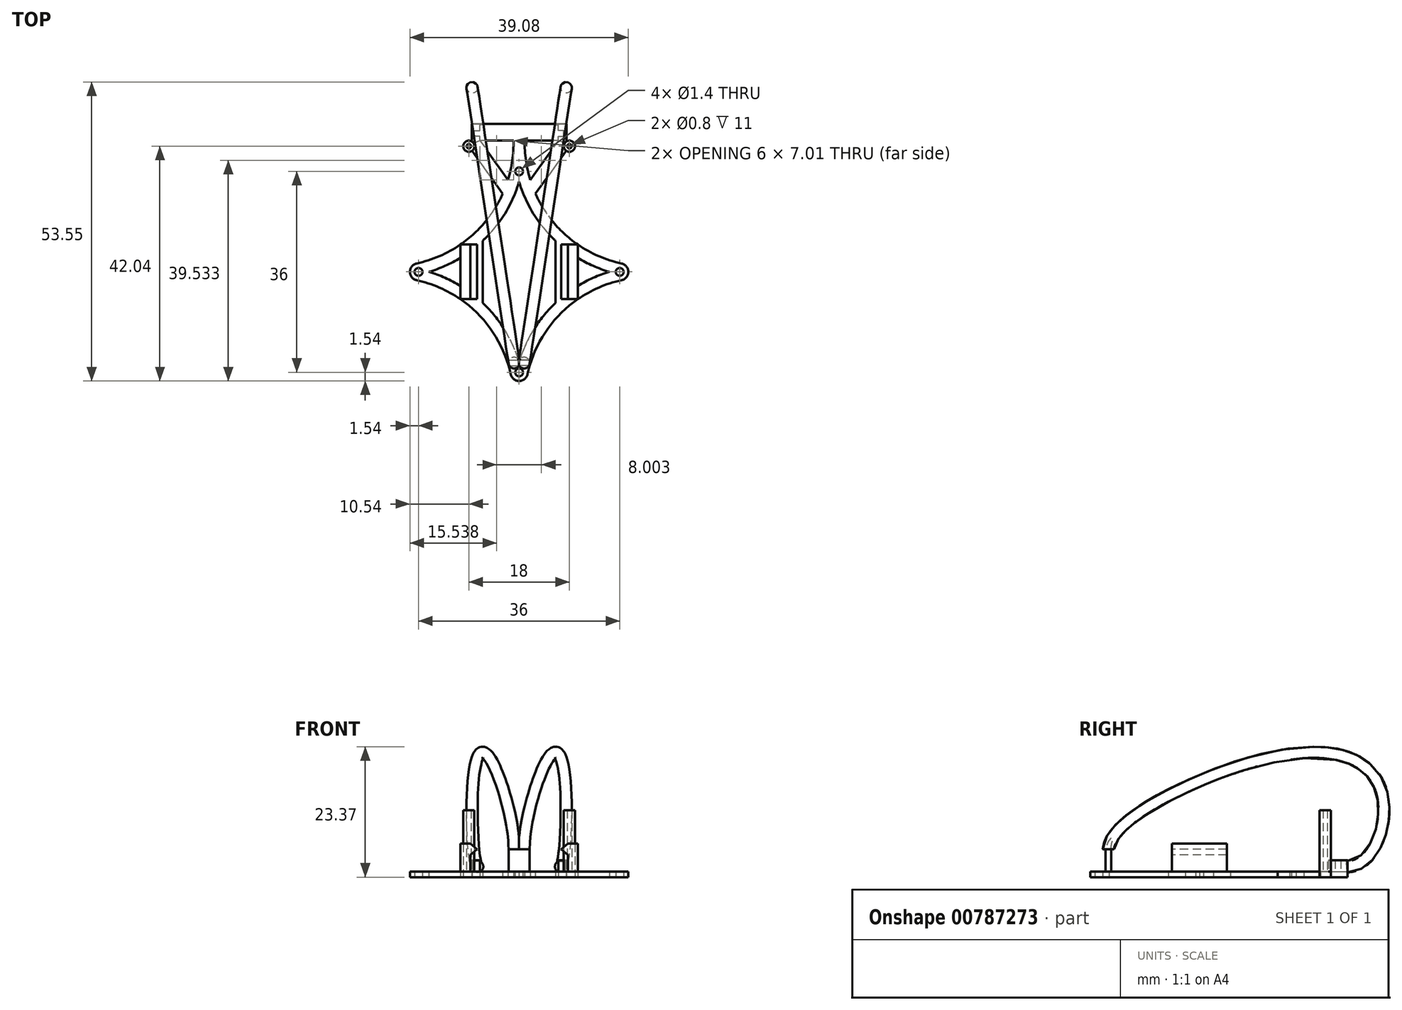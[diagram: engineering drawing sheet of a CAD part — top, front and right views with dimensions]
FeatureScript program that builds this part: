
annotation { "Feature Type Name" : "Feature", "Feature Type Description" : "" }
export const myFeature = defineFeature(function(context is Context, id is Id, definition is map)
    precondition{}
    {
        {
            var Q0;
            Q0=qCreatedBy(makeId("Top.planeOp"),FACE);
            var sketch = newSketch(context, id + "F0", { "sketchPlane" : qUnion([Q0])});
            skCircle(sketch, "E0", {"center": v(0, 18) * mm, "radius": 0.7 * mm});
            skCircle(sketch, "E1", {"center": v(18, 0) * mm, "radius": 0.7 * mm});
            skCircle(sketch, "E2", {"center": v(0, -18) * mm, "radius": 0.7 * mm});
            skCircle(sketch, "E3", {"center": v(-18, 0) * mm, "radius": 0.7 * mm});
            skLineSegment(sketch, "E4.bottom", {"start": v(23, 23) * mm, "end": v(-23, 23) * mm, "construction": true});
            skLineSegment(sketch, "E4.top", {"start": v(23, -23) * mm, "end": v(-23, -23) * mm, "construction": true});
            skLineSegment(sketch, "E4.left", {"start": v(23, 23) * mm, "end": v(23, -23) * mm, "construction": true});
            skLineSegment(sketch, "E4.right", {"start": v(-23, 23) * mm, "end": v(-23, -23) * mm, "construction": true});
            skPoint(sketch, "E4.middle", {"position": v(0, 0) * mm});
            skArc(sketch, "E5", {"start": v(1, 23.5) * mm, "mid": v(1.21, 19.95) * mm, "end": v(1.99, 16.49) * mm});
            skArc(sketch, "E6", {"start": v(18.33, -1.5) * mm, "mid": v(7.44, -7.44) * mm, "end": v(1.5, -18.33) * mm});
            skArc(sketch, "E7", {"start": v(-1.5, -18.33) * mm, "mid": v(-7.44, -7.44) * mm, "end": v(-18.33, -1.5) * mm});
            skArc(sketch, "E8", {"start": v(-18.33, 1.5) * mm, "mid": v(-9.14, 5.92) * mm, "end": v(-2.93, 14) * mm});
            skPoint(sketch, "E9", {"position": v(0, 35.14) * mm});
            skArc(sketch, "E10", {"start": v(0, 16.14) * mm, "mid": v(2.55, 10.43) * mm, "end": v(6.5, 5.57) * mm});
            skArc(sketch, "E11", {"start": v(0, 16.14) * mm, "mid": v(-2.55, 10.43) * mm, "end": v(-6.5, 5.57) * mm});
            skArc(sketch, "E12", {"start": v(-16.14, 0) * mm, "mid": v(-13.24, -1.07) * mm, "end": v(-10.5, -2.51) * mm});
            skArc(sketch, "E13", {"start": v(16.14, 0) * mm, "mid": v(13.24, -1.07) * mm, "end": v(10.5, -2.51) * mm});
            skArc(sketch, "E14", {"start": v(-1.5, -18.33) * mm, "mid": v(0, -19.54) * mm, "end": v(1.5, -18.33) * mm});
            skArc(sketch, "E15", {"start": v(-18.33, -1.5) * mm, "mid": v(-19.54, 0) * mm, "end": v(-18.33, 1.5) * mm});
            skArc(sketch, "E16", {"start": v(18.33, -1.5) * mm, "mid": v(19.54, 0) * mm, "end": v(18.33, 1.5) * mm});
            skLineSegment(sketch, "E17", {"start": v(-10.5, 2.51) * mm, "end": v(-10.5, -2.51) * mm});
            skLineSegment(sketch, "E18", {"start": v(-6.5, -5.57) * mm, "end": v(-6.5, 5.57) * mm});
            skLineSegment(sketch, "E19", {"start": v(10.5, 2.51) * mm, "end": v(10.5, -2.51) * mm});
            skLineSegment(sketch, "E20", {"start": v(6.5, -5.57) * mm, "end": v(6.5, 5.57) * mm});
            skPoint(sketch, "E21", {"position": v(-10.5, 0) * mm});
            skPoint(sketch, "E22", {"position": v(-6.5, 0) * mm});
            skPoint(sketch, "E23", {"position": v(6.5, 0) * mm});
            skPoint(sketch, "E24", {"position": v(10.5, 0) * mm});
            skArc(sketch, "E25.trimOffspring", {"start": v(-10.5, 2.51) * mm, "mid": v(-13.24, 1.07) * mm, "end": v(-16.14, 0) * mm});
            skArc(sketch, "E26.trimOffspring", {"start": v(-6.5, -5.57) * mm, "mid": v(-2.55, -10.43) * mm, "end": v(0, -16.14) * mm});
            skArc(sketch, "E27.trimOffspring", {"start": v(6.5, -5.57) * mm, "mid": v(2.55, -10.43) * mm, "end": v(0, -16.14) * mm});
            skArc(sketch, "E28.trimOffspring", {"start": v(10.5, 2.51) * mm, "mid": v(13.24, 1.07) * mm, "end": v(16.14, 0) * mm});
            skLineSegment(sketch, "E29.bottom", {"start": v(7, 23.5) * mm, "end": v(1, 23.5) * mm});
            skLineSegment(sketch, "E29.top", {"start": v(8.5, 26.5) * mm, "end": v(-8.5, 26.5) * mm});
            skLineSegment(sketch, "E29.left", {"start": v(8.5, 23.37) * mm, "end": v(8.5, 26.5) * mm});
            skLineSegment(sketch, "E29.right", {"start": v(-8.5, 23.37) * mm, "end": v(-8.5, 26.5) * mm});
            skPoint(sketch, "E29.middle", {"position": v(0, 25) * mm});
            skLineSegment(sketch, "E30", {"start": v(-7, 23.5) * mm, "end": v(-1.99, 16.49) * mm});
            skLineSegment(sketch, "E31", {"start": v(7, 23.5) * mm, "end": v(1.99, 16.49) * mm});
            skArc(sketch, "E32.trimOffspring", {"start": v(-1.99, 16.49) * mm, "mid": v(-1.21, 19.95) * mm, "end": v(-1, 23.5) * mm});
            skArc(sketch, "E33.trimOffspring", {"start": v(2.93, 14) * mm, "mid": v(9.14, 5.92) * mm, "end": v(18.33, 1.5) * mm});
            skLineSegment(sketch, "E34.trimOffspring", {"start": v(-1, 23.5) * mm, "end": v(-7, 23.5) * mm});
            skArc(sketch, "E35", {"start": v(-8.5, 23.37) * mm, "mid": v(-10, 22.45) * mm, "end": v(-8.42, 21.69) * mm});
            skLineSegment(sketch, "E36", {"start": v(-2.93, 14) * mm, "end": v(-8.42, 21.69) * mm});
            skPoint(sketch, "E37.orphan", {"position": v(-8.5, 23.5) * mm});
            skArc(sketch, "E38.MirrorC", {"start": v(8.5, 23.37) * mm, "mid": v(10, 22.45) * mm, "end": v(8.42, 21.69) * mm});
            skLineSegment(sketch, "E39.trimOffspring", {"start": v(8.42, 21.69) * mm, "end": v(2.93, 14) * mm});
            skPoint(sketch, "E40.orphan", {"position": v(8.5, 23.5) * mm});
            skSolve(sketch);
        }
        {
            var Q0;
            Q0 = qSketchRegion(id + "F0", true);
            extrude(context, id + "F1", {"entities" : qUnion([Q0]), "depth" : 1 * mm, "offsetDistance" : 25 * mm});
        }
        {
            var Q0;
            Q0=makeQuery(id+"F1.opExtrude","CAP_FACE",FACE,{"disambiguationData":[OSD([sQuery(id+"F0.wireOp",EDGE,"E0"),sQuery(id+"F0.wireOp",EDGE,"E1"),sQuery(id+"F0.wireOp",EDGE,"E2"),sQuery(id+"F0.wireOp",EDGE,"E3"),sQuery(id+"F0.wireOp",EDGE,"E5"),sQuery(id+"F0.wireOp",EDGE,"E6"),sQuery(id+"F0.wireOp",EDGE,"E7"),sQuery(id+"F0.wireOp",EDGE,"E8"),sQuery(id+"F0.wireOp",EDGE,"E10"),sQuery(id+"F0.wireOp",EDGE,"E11"),sQuery(id+"F0.wireOp",EDGE,"E12"),sQuery(id+"F0.wireOp",EDGE,"E13"),sQuery(id+"F0.wireOp",EDGE,"E14"),sQuery(id+"F0.wireOp",EDGE,"E15"),sQuery(id+"F0.wireOp",EDGE,"E16"),sQuery(id+"F0.wireOp",EDGE,"E17"),sQuery(id+"F0.wireOp",EDGE,"E18"),sQuery(id+"F0.wireOp",EDGE,"E19"),sQuery(id+"F0.wireOp",EDGE,"E20"),sQuery(id+"F0.wireOp",EDGE,"E25.trimOffspring"),sQuery(id+"F0.wireOp",EDGE,"E26.trimOffspring"),sQuery(id+"F0.wireOp",EDGE,"E27.trimOffspring"),sQuery(id+"F0.wireOp",EDGE,"E28.trimOffspring"),sQuery(id+"F0.wireOp",EDGE,"E29.bottom"),sQuery(id+"F0.wireOp",EDGE,"E29.top"),sQuery(id+"F0.wireOp",EDGE,"E29.left"),sQuery(id+"F0.wireOp",EDGE,"E29.right"),sQuery(id+"F0.wireOp",EDGE,"qweFKNHt-NEOd-9uf7-BY6i-RgVFOMZ5KD8T"),sQuery(id+"F0.wireOp",EDGE,"E30"),sQuery(id+"F0.wireOp",EDGE,"MFzCZS1V-zBad-YQFP-DdxK-P2Gc9sIkp1Xx"),sQuery(id+"F0.wireOp",EDGE,"E31"),sQuery(id+"F0.wireOp",EDGE,"E32.trimOffspring"),sQuery(id+"F0.wireOp",EDGE,"E33.trimOffspring"),sQuery(id+"F0.wireOp",EDGE,"E34.trimOffspring")])],"isStart":false});
            var sketch = newSketch(context, id + "F2", { "sketchPlane" : qUnion([Q0])});
            skLineSegment(sketch, "E41", {"start": v(-7, 26.5) * mm, "end": v(-8.5, 26.5) * mm});
            skLineSegment(sketch, "E42", {"start": v(-8.5, 26.5) * mm, "end": v(-8.5, 23) * mm});
            skLineSegment(sketch, "E43", {"start": v(-8.5, 23) * mm, "end": v(-7, 23.5) * mm});
            skLineSegment(sketch, "E44", {"start": v(-7, 23.5) * mm, "end": v(-7, 24.3) * mm});
            skLineSegment(sketch, "E45", {"start": v(-7, 24.3) * mm, "end": v(-8, 24.3) * mm});
            skLineSegment(sketch, "E46", {"start": v(-8, 24.3) * mm, "end": v(-8, 25.3) * mm});
            skLineSegment(sketch, "E47", {"start": v(-8, 25.3) * mm, "end": v(-7, 25.3) * mm});
            skLineSegment(sketch, "E48", {"start": v(-7, 25.3) * mm, "end": v(-7, 26.5) * mm});
            skLineSegment(sketch, "E49.MirrorCS", {"start": v(8.5, 26.5) * mm, "end": v(8.5, 23) * mm});
            skLineSegment(sketch, "E50.MirrorCS", {"start": v(8, 24.3) * mm, "end": v(8, 25.3) * mm});
            skLineSegment(sketch, "E51.MirrorCS", {"start": v(7, 25.3) * mm, "end": v(7, 26.5) * mm});
            skLineSegment(sketch, "E52.MirrorCS", {"start": v(7, 23.5) * mm, "end": v(7, 24.3) * mm});
            skLineSegment(sketch, "E53.MirrorCS", {"start": v(7, 24.3) * mm, "end": v(8, 24.3) * mm});
            skLineSegment(sketch, "E54.MirrorCS", {"start": v(7, 26.5) * mm, "end": v(8.5, 26.5) * mm});
            skLineSegment(sketch, "E55.MirrorCS", {"start": v(8, 25.3) * mm, "end": v(7, 25.3) * mm});
            skLineSegment(sketch, "E56.MirrorCS", {"start": v(8.5, 23) * mm, "end": v(7, 23.5) * mm});
            skSolve(sketch);
        }
        {
            var Q0;
            Q0 = qSketchRegion(id + "F2", true);
            extrude(context, id + "F3", {"entities" : qUnion([Q0]), "operationType" : NewBodyOperationType.ADD, "depth" : 2 * mm, "offsetDistance" : 25 * mm});
        }
        {
            var Q0;
            Q0=makeQuery(id+"F1.opExtrude","CAP_FACE",FACE,{"disambiguationData":[OSD([sQuery(id+"F0.wireOp",EDGE,"E0"),sQuery(id+"F0.wireOp",EDGE,"E1"),sQuery(id+"F0.wireOp",EDGE,"E2"),sQuery(id+"F0.wireOp",EDGE,"E3"),sQuery(id+"F0.wireOp",EDGE,"E5"),sQuery(id+"F0.wireOp",EDGE,"E6"),sQuery(id+"F0.wireOp",EDGE,"E7"),sQuery(id+"F0.wireOp",EDGE,"E8"),sQuery(id+"F0.wireOp",EDGE,"E10"),sQuery(id+"F0.wireOp",EDGE,"E11"),sQuery(id+"F0.wireOp",EDGE,"E12"),sQuery(id+"F0.wireOp",EDGE,"E13"),sQuery(id+"F0.wireOp",EDGE,"E14"),sQuery(id+"F0.wireOp",EDGE,"E15"),sQuery(id+"F0.wireOp",EDGE,"E16"),sQuery(id+"F0.wireOp",EDGE,"E17"),sQuery(id+"F0.wireOp",EDGE,"E18"),sQuery(id+"F0.wireOp",EDGE,"E19"),sQuery(id+"F0.wireOp",EDGE,"E20"),sQuery(id+"F0.wireOp",EDGE,"E25.trimOffspring"),sQuery(id+"F0.wireOp",EDGE,"E26.trimOffspring"),sQuery(id+"F0.wireOp",EDGE,"E27.trimOffspring"),sQuery(id+"F0.wireOp",EDGE,"E28.trimOffspring"),sQuery(id+"F0.wireOp",EDGE,"E29.bottom"),sQuery(id+"F0.wireOp",EDGE,"E29.top"),sQuery(id+"F0.wireOp",EDGE,"E29.left"),sQuery(id+"F0.wireOp",EDGE,"E29.right"),sQuery(id+"F0.wireOp",EDGE,"E30"),sQuery(id+"F0.wireOp",EDGE,"E31"),sQuery(id+"F0.wireOp",EDGE,"E32.trimOffspring"),sQuery(id+"F0.wireOp",EDGE,"E33.trimOffspring"),sQuery(id+"F0.wireOp",EDGE,"E34.trimOffspring"),sQuery(id+"F0.wireOp",EDGE,"E35"),sQuery(id+"F0.wireOp",EDGE,"E36"),sQuery(id+"F0.wireOp",EDGE,"E38.MirrorC"),sQuery(id+"F0.wireOp",EDGE,"E39.trimOffspring")])],"isStart":false});
            var sketch = newSketch(context, id + "F4", { "sketchPlane" : qUnion([Q0])});
            skCircle(sketch, "E57", {"center": v(-9, 22.5) * mm, "radius": 1 * mm});
            skCircle(sketch, "E58", {"center": v(-9, 22.5) * mm, "radius": 0.4 * mm});
            skCircle(sketch, "E59.MirrorC", {"center": v(9, 22.5) * mm, "radius": 0.4 * mm});
            skCircle(sketch, "E60.MirrorC", {"center": v(9, 22.5) * mm, "radius": 1 * mm});
            skSolve(sketch);
        }
        {
            var Q0;
            Q0 = qSketchRegion(id + "F4", true);
            extrude(context, id + "F5", {"entities" : qUnion([Q0]), "operationType" : NewBodyOperationType.ADD, "depth" : 11 * mm, "offsetDistance" : 25 * mm});
        }
        {
            var Q0;
            {var subQ0=sQuery(id+"F0.wireOp",EDGE,"E36");var subQ1=sQuery(id+"F0.wireOp",EDGE,"E35");var subQ2=sQuery(id+"F0.wireOp",EDGE,"E34.trimOffspring");var subQ3=sQuery(id+"F0.wireOp",EDGE,"E33.trimOffspring");var subQ4=sQuery(id+"F0.wireOp",EDGE,"E32.trimOffspring");var subQ5=sQuery(id+"F0.wireOp",EDGE,"E18");var subQ6=sQuery(id+"F0.wireOp",EDGE,"E39.trimOffspring");var subQ7=sQuery(id+"F0.wireOp",EDGE,"E29.top");var subQ8=sQuery(id+"F0.wireOp",EDGE,"E38.MirrorC");var subQ9=sQuery(id+"F0.wireOp",EDGE,"E29.bottom");var subQ10=sQuery(id+"F0.wireOp",EDGE,"E28.trimOffspring");var subQ11=sQuery(id+"F0.wireOp",EDGE,"E27.trimOffspring");var subQ12=sQuery(id+"F0.wireOp",EDGE,"E26.trimOffspring");var subQ13=sQuery(id+"F0.wireOp",EDGE,"E31");var subQ14=sQuery(id+"F0.wireOp",EDGE,"E30");var subQ15=sQuery(id+"F0.wireOp",EDGE,"E10");var subQ16=sQuery(id+"F0.wireOp",EDGE,"E8");var subQ17=sQuery(id+"F0.wireOp",EDGE,"E7");var subQ18=sQuery(id+"F0.wireOp",EDGE,"E6");var subQ19=sQuery(id+"F0.wireOp",EDGE,"E5");var subQ20=sQuery(id+"F0.wireOp",EDGE,"E11");var subQ21=sQuery(id+"F0.wireOp",EDGE,"E0");var subQ22=sQuery(id+"F0.wireOp",EDGE,"E3");var subQ23=sQuery(id+"F0.wireOp",EDGE,"E1");var subQ24=sQuery(id+"F0.wireOp",EDGE,"E2");var subQ25=sQuery(id+"F0.wireOp",EDGE,"E12");var subQ26=sQuery(id+"F0.wireOp",EDGE,"E13");var subQ27=sQuery(id+"F0.wireOp",EDGE,"E14");var subQ28=sQuery(id+"F0.wireOp",EDGE,"E15");var subQ29=sQuery(id+"F0.wireOp",EDGE,"E16");var subQ30=sQuery(id+"F0.wireOp",EDGE,"E17");var subQ31=sQuery(id+"F0.wireOp",EDGE,"E19");var subQ32=sQuery(id+"F0.wireOp",EDGE,"E20");var subQ33=sQuery(id+"F0.wireOp",EDGE,"E25.trimOffspring");Q0=makeQuery(id+"F5.boolean.opBoolean","SPLIT",FACE,{"disambiguationData":[TD([makeQuery(id+"F1.opExtrude","SWEPT_FACE",FACE,{"disambiguationData":[OSD([subQ21])]})])],"derivedFrom":makeQuery(id+"F1.opExtrude","CAP_FACE",FACE,{"disambiguationData":[OSD([subQ21,subQ23,subQ24,subQ22,subQ19,subQ18,subQ17,subQ16,subQ15,subQ20,subQ25,subQ26,subQ27,subQ28,subQ29,subQ30,subQ5,subQ31,subQ32,subQ33,subQ12,subQ11,subQ10,subQ9,subQ7,sQuery(id+"F0.wireOp",EDGE,"E29.left"),sQuery(id+"F0.wireOp",EDGE,"E29.right"),subQ14,subQ13,subQ4,subQ3,subQ2,subQ1,subQ0,subQ8,subQ6])],"isStart":false})});}
            var sketch = newSketch(context, id + "F6", { "sketchPlane" : qUnion([Q0])});
            skLineSegment(sketch, "E61.bottom", {"start": v(-10.5, 4.9) * mm, "end": v(-8.75, 4.9) * mm});
            skLineSegment(sketch, "E61.top", {"start": v(-10.5, -4.9) * mm, "end": v(-8.75, -4.9) * mm});
            skLineSegment(sketch, "E61.left", {"start": v(-10.5, 4.9) * mm, "end": v(-10.5, -4.9) * mm});
            skLineSegment(sketch, "E61.right", {"start": v(-8.75, 4.9) * mm, "end": v(-8.75, -4.9) * mm});
            skLineSegment(sketch, "E62.MirrorCS", {"start": v(10.5, 4.9) * mm, "end": v(8.75, 4.9) * mm});
            skLineSegment(sketch, "E63.MirrorCS", {"start": v(10.5, -4.9) * mm, "end": v(8.75, -4.9) * mm});
            skLineSegment(sketch, "E64.MirrorCS", {"start": v(10.5, 4.9) * mm, "end": v(10.5, -4.9) * mm});
            skLineSegment(sketch, "E65.MirrorCS", {"start": v(8.75, 4.9) * mm, "end": v(8.75, -4.9) * mm});
            skSolve(sketch);
        }
        {
            var Q0;
            Q0 = qSketchRegion(id + "F6", true);
            extrude(context, id + "F7", {"entities" : qUnion([Q0]), "operationType" : NewBodyOperationType.ADD, "depth" : 5 * mm, "offsetDistance" : 25 * mm});
        }
        {
            var Q0;
            Q0=makeQuery(id+"F7.opExtrude","SWEPT_FACE",FACE,{"disambiguationData":[OSD([sQuery(id+"F6.wireOp",EDGE,"E61.top")])]});
            var sketch = newSketch(context, id + "F8", { "sketchPlane" : qUnion([Q0])});
            skLineSegment(sketch, "E66", {"start": v(-8.75, 6) * mm, "end": v(-7.55, 5) * mm});
            skLineSegment(sketch, "E67", {"start": v(-7.55, 5) * mm, "end": v(-8.75, 4) * mm});
            skLineSegment(sketch, "E68", {"start": v(-8.75, 4) * mm, "end": v(-8.75, 6) * mm});
            skLineSegment(sketch, "E69.MirrorCS", {"start": v(8.75, 6) * mm, "end": v(7.55, 5) * mm});
            skLineSegment(sketch, "E70.MirrorCS", {"start": v(8.75, 4) * mm, "end": v(8.75, 6) * mm});
            skLineSegment(sketch, "E71.MirrorCS", {"start": v(7.55, 5) * mm, "end": v(8.75, 4) * mm});
            skSolve(sketch);
        }
        {
            var Q0;
            Q0 = qSketchRegion(id + "F8", true);
            var Q1;
            Q1=makeQuery(id+"F7.opExtrude","CAP_VERTEX",VERTEX,{"disambiguationData":[OSD([sQuery(id+"F6.wireOp",EDGE,"E61.bottom"),sQuery(id+"F6.wireOp",EDGE,"E61.right")])],"isStart":false});
            extrude(context, id + "F9", {"entities" : qUnion([Q0]), "operationType" : NewBodyOperationType.ADD, "endBound" : BoundingType.UP_TO_VERTEX, "oppositeDirection" : true, "depth" : 10 * mm, "endBoundEntityVertex" : qUnion([Q1]), "offsetDistance" : 25 * mm});
        }
        {
            var Q0;
            {var subQ1=sQuery(id+"F0.wireOp",EDGE,"E38.MirrorC");var subQ4=sQuery(id+"F0.wireOp",EDGE,"E36");var subQ7=sQuery(id+"F0.wireOp",EDGE,"E35");var subQ10=sQuery(id+"F0.wireOp",EDGE,"E34.trimOffspring");var subQ13=sQuery(id+"F0.wireOp",EDGE,"E33.trimOffspring");var subQ16=sQuery(id+"F0.wireOp",EDGE,"E32.trimOffspring");var subQ19=sQuery(id+"F0.wireOp",EDGE,"E29.right");var subQ22=sQuery(id+"F0.wireOp",EDGE,"E29.left");var subQ24=sQuery(id+"F0.wireOp",EDGE,"E39.trimOffspring");var subQ28=sQuery(id+"F0.wireOp",EDGE,"E29.top");var subQ31=sQuery(id+"F0.wireOp",EDGE,"E29.bottom");var subQ36=sQuery(id+"F0.wireOp",EDGE,"E27.trimOffspring");var subQ39=sQuery(id+"F0.wireOp",EDGE,"E26.trimOffspring");var subQ42=sQuery(id+"F0.wireOp",EDGE,"E14");var subQ44=sQuery(id+"F0.wireOp",EDGE,"E10");var subQ46=sQuery(id+"F0.wireOp",EDGE,"E8");var subQ48=sQuery(id+"F0.wireOp",EDGE,"E7");var subQ50=sQuery(id+"F0.wireOp",EDGE,"E6");var subQ52=sQuery(id+"F0.wireOp",EDGE,"E31");var subQ54=sQuery(id+"F0.wireOp",EDGE,"E11");var subQ56=sQuery(id+"F0.wireOp",EDGE,"E0");var subQ57=makeQuery(id+"F1.opExtrude","SWEPT_FACE",FACE,{"disambiguationData":[OSD([subQ56])]});var subQ58=sQuery(id+"F0.wireOp",EDGE,"E30");var subQ59=sQuery(id+"F0.wireOp",EDGE,"E28.trimOffspring");var subQ60=sQuery(id+"F0.wireOp",EDGE,"E25.trimOffspring");var subQ61=sQuery(id+"F0.wireOp",EDGE,"E20");var subQ62=sQuery(id+"F0.wireOp",EDGE,"E19");var subQ63=sQuery(id+"F0.wireOp",EDGE,"E18");var subQ64=sQuery(id+"F0.wireOp",EDGE,"E17");var subQ65=sQuery(id+"F0.wireOp",EDGE,"E16");var subQ66=sQuery(id+"F0.wireOp",EDGE,"E15");var subQ67=sQuery(id+"F0.wireOp",EDGE,"E13");var subQ68=sQuery(id+"F0.wireOp",EDGE,"E12");var subQ69=sQuery(id+"F0.wireOp",EDGE,"E5");var subQ70=sQuery(id+"F0.wireOp",EDGE,"E3");var subQ71=sQuery(id+"F0.wireOp",EDGE,"E2");var subQ72=sQuery(id+"F0.wireOp",EDGE,"E1");var subQ73=makeQuery(id+"F1.opExtrude","CAP_FACE",FACE,{"disambiguationData":[OSD([subQ56,subQ72,subQ71,subQ70,subQ69,subQ50,subQ48,subQ46,subQ44,subQ54,subQ68,subQ67,subQ42,subQ66,subQ65,subQ64,subQ63,subQ62,subQ61,subQ60,subQ39,subQ36,subQ59,subQ31,subQ28,subQ22,subQ19,subQ58,subQ52,subQ16,subQ13,subQ10,subQ7,subQ4,subQ1,subQ24])],"isStart":false});Q0=makeQuery(id+"F7.boolean.opBoolean","SPLIT",FACE,{"disambiguationData":[TD([subQ57])],"derivedFrom":makeQuery(id+"F5.boolean.opBoolean","SPLIT",FACE,{"disambiguationData":[TD([subQ57])],"derivedFrom":subQ73})});}
            var sketch = newSketch(context, id + "F10", { "sketchPlane" : qUnion([Q0])});
            skLineSegment(sketch, "E72.bottom", {"start": v(-1.9, -16.8) * mm, "end": v(1.9, -16.8) * mm});
            skLineSegment(sketch, "E72.top", {"start": v(-1.9, -15.8) * mm, "end": v(1.9, -15.8) * mm});
            skLineSegment(sketch, "E72.left", {"start": v(-1.9, -16.8) * mm, "end": v(-1.9, -15.8) * mm});
            skLineSegment(sketch, "E72.right", {"start": v(1.9, -16.8) * mm, "end": v(1.9, -15.8) * mm});
            skSolve(sketch);
        }
        {
            var Q0;
            Q0 = qSketchRegion(id + "F10", true);
            extrude(context, id + "F11", {"entities" : qUnion([Q0]), "operationType" : NewBodyOperationType.ADD, "depth" : 4 * mm, "offsetDistance" : 25 * mm});
        }
        {
            var Q0;
            Q0=makeQuery(id+"F11.opExtrude","CAP_VERTEX",VERTEX,{"disambiguationData":[OSD([sQuery(id+"F0.wireOp",EDGE,"E7"),sQuery(id+"F10.wireOp",EDGE,"E72.bottom"),sQuery(id+"F10.wireOp",EDGE,"E72.left")])],"isStart":true});
            var Q1;
            Q1=makeQuery(id+"F11.opExtrude","CAP_VERTEX",VERTEX,{"disambiguationData":[OSD([sQuery(id+"F0.wireOp",EDGE,"E7"),sQuery(id+"F10.wireOp",EDGE,"E72.bottom"),sQuery(id+"F10.wireOp",EDGE,"E72.left")])],"isStart":false});
            var Q2;
            Q2=makeQuery(id+"F1.opExtrude","CAP_VERTEX",VERTEX,{"disambiguationData":[OSD([sQuery(id+"F0.wireOp",EDGE,"E29.top"),sQuery(id+"F0.wireOp",EDGE,"E29.right")])],"isStart":true});
            cPlane(context, id + "F12", {"entities" : qUnion([Q0, Q1, Q2]), "cplaneType" : CPlaneType.THREE_POINT, "offset" : 25 * mm, "width" : 150 * mm, "height" : 150 * mm});
        }
        {
            var Q0;
            Q0=qCreatedBy(id+"F12.planeOp",FACE);
            var sketch = newSketch(context, id + "F13", { "sketchPlane" : qUnion([Q0])});
            skFitSpline(sketch, "E73", {"points": [v(27.14, 1.52) * mm, v(34.12, 13.97) * mm, v(24.34, 22.52) * mm, v(-4.65, 15.23) * mm, v(-16.32, 5) * mm], "startDerivative": vector(68.56, 0.12) * mm, "endDerivative": vector(-2.87, -43.18) * mm});
            skSolve(sketch);
        }
        {
            var Q0;
            Q0=makeQuery(id+"F11.opExtrude","CAP_FACE",FACE,{"disambiguationData":[OSD([sQuery(id+"F10.wireOp",EDGE,"E72.bottom"),sQuery(id+"F10.wireOp",EDGE,"E72.top"),sQuery(id+"F10.wireOp",EDGE,"E72.left"),sQuery(id+"F10.wireOp",EDGE,"E72.right")])],"isStart":false});
            var sketch = newSketch(context, id + "F14", { "sketchPlane" : qUnion([Q0])});
            skCircle(sketch, "E74", {"center": v(-0.9, -16.3) * mm, "radius": 1 * mm});
            skPoint(sketch, "E75", {"position": v(-1.9, -16.3) * mm});
            skSolve(sketch);
        }
        {
            var Q0;
            Q0 = qSketchRegion(id + "F14", true);
            var Q1;
            Q1 = qConstructionFilter(qBodyType(qCreatedBy(id + "F13" ,EDGE), BodyType.WIRE), ConstructionObject.NO);
            sweep(context, id + "F15", {"operationType" : NewBodyOperationType.ADD, "profiles" : qUnion([Q0]), "path" : qUnion([Q1])});
        }
        {
            var Q0;
            Q0=makeQuery(id+"F1.opExtrude","SWEPT_BODY",BODY,{"disambiguationData":[OSD([sQuery(id+"F0.wireOp",EDGE,"E0"),sQuery(id+"F0.wireOp",EDGE,"E1"),sQuery(id+"F0.wireOp",EDGE,"E2"),sQuery(id+"F0.wireOp",EDGE,"E3"),sQuery(id+"F0.wireOp",EDGE,"E5"),sQuery(id+"F0.wireOp",EDGE,"E6"),sQuery(id+"F0.wireOp",EDGE,"E7"),sQuery(id+"F0.wireOp",EDGE,"E8"),sQuery(id+"F0.wireOp",EDGE,"E10"),sQuery(id+"F0.wireOp",EDGE,"E11"),sQuery(id+"F0.wireOp",EDGE,"E12"),sQuery(id+"F0.wireOp",EDGE,"E13"),sQuery(id+"F0.wireOp",EDGE,"E14"),sQuery(id+"F0.wireOp",EDGE,"E15"),sQuery(id+"F0.wireOp",EDGE,"E16"),sQuery(id+"F0.wireOp",EDGE,"E17"),sQuery(id+"F0.wireOp",EDGE,"E18"),sQuery(id+"F0.wireOp",EDGE,"E19"),sQuery(id+"F0.wireOp",EDGE,"E20"),sQuery(id+"F0.wireOp",EDGE,"E25.trimOffspring"),sQuery(id+"F0.wireOp",EDGE,"E26.trimOffspring"),sQuery(id+"F0.wireOp",EDGE,"E27.trimOffspring"),sQuery(id+"F0.wireOp",EDGE,"E28.trimOffspring"),sQuery(id+"F0.wireOp",EDGE,"E29.bottom"),sQuery(id+"F0.wireOp",EDGE,"E29.top"),sQuery(id+"F0.wireOp",EDGE,"E29.left"),sQuery(id+"F0.wireOp",EDGE,"E29.right"),sQuery(id+"F0.wireOp",EDGE,"E30"),sQuery(id+"F0.wireOp",EDGE,"E31"),sQuery(id+"F0.wireOp",EDGE,"E32.trimOffspring"),sQuery(id+"F0.wireOp",EDGE,"E33.trimOffspring"),sQuery(id+"F0.wireOp",EDGE,"E34.trimOffspring"),sQuery(id+"F0.wireOp",EDGE,"E35"),sQuery(id+"F0.wireOp",EDGE,"E36"),sQuery(id+"F0.wireOp",EDGE,"E38.MirrorC"),sQuery(id+"F0.wireOp",EDGE,"E39.trimOffspring")])]});
            var Q1;
            Q1=qCreatedBy(makeId("Right.planeOp"),FACE);
            mirror(context, id + "F16", {"operationType" : NewBodyOperationType.ADD, "entities" : qUnion([Q0]), "mirrorPlane" : qUnion([Q1])});
        }
    });
